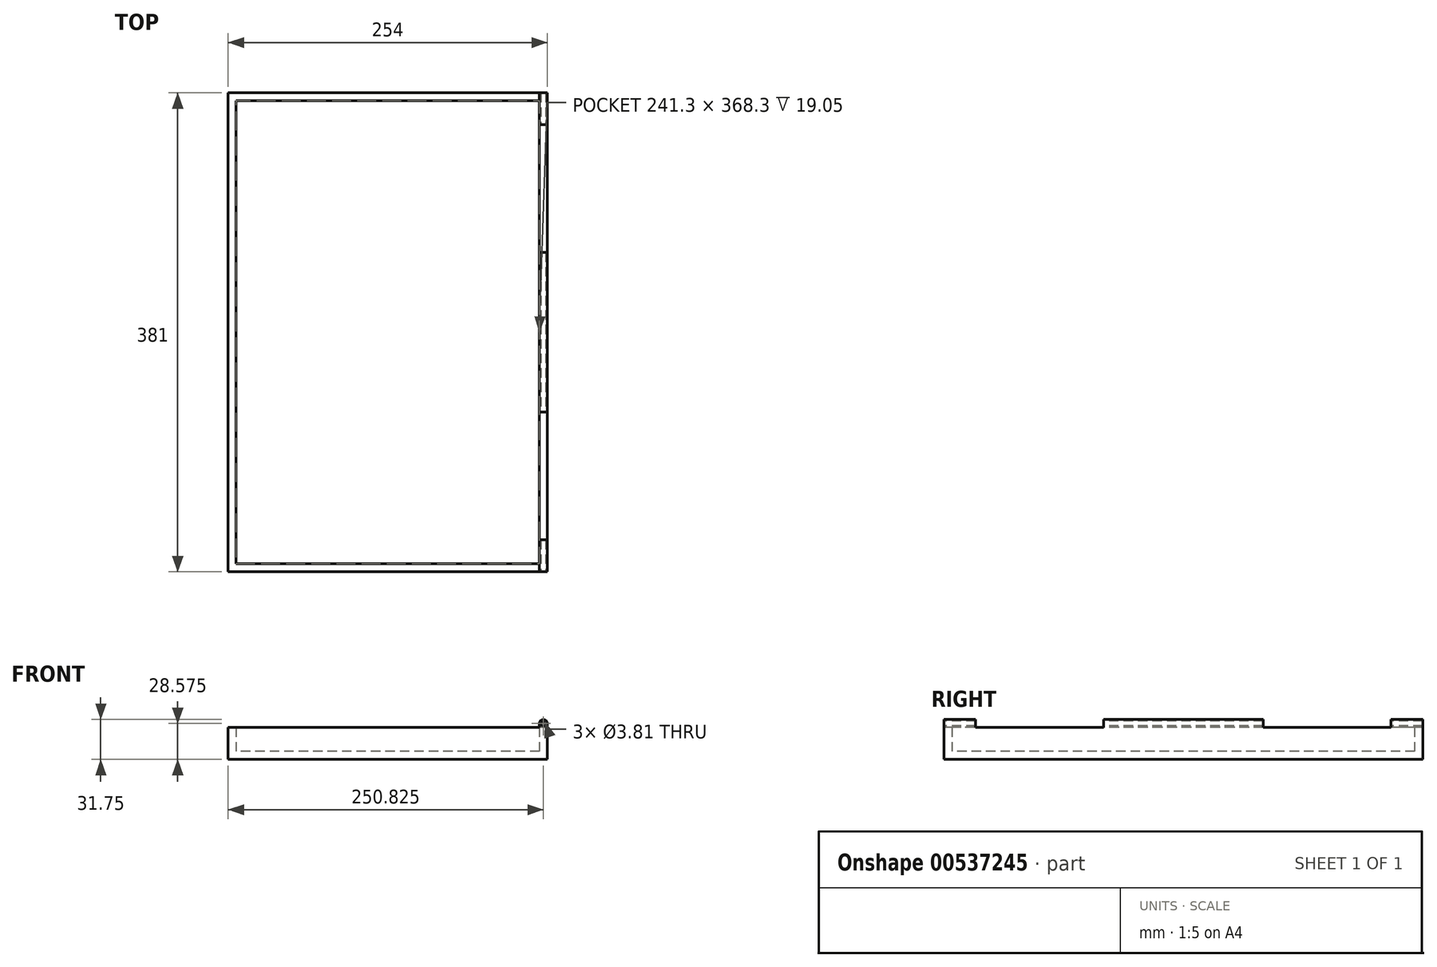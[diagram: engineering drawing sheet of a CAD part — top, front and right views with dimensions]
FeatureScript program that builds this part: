
annotation { "Feature Type Name" : "Feature", "Feature Type Description" : "" }
export const myFeature = defineFeature(function(context is Context, id is Id, definition is map)
    precondition{}
    {
        {
            var Q0;
            Q0=qCreatedBy(makeId("Top.planeOp"),FACE);
            var sketch = newSketch(context, id + "F0", { "sketchPlane" : qUnion([Q0])});
            skLineSegment(sketch, "E0.bottom", {"start": v(127, 190.5) * mm, "end": v(-127, 190.5) * mm});
            skLineSegment(sketch, "E0.top", {"start": v(127, -190.5) * mm, "end": v(-127, -190.5) * mm});
            skLineSegment(sketch, "E0.left", {"start": v(127, 190.5) * mm, "end": v(127, -190.5) * mm});
            skLineSegment(sketch, "E0.right", {"start": v(-127, 190.5) * mm, "end": v(-127, -190.5) * mm});
            skPoint(sketch, "E0.middle", {"position": v(0, 0) * mm});
            skLineSegment(sketch, "E1.0", {"start": v(120.65, -184.15) * mm, "end": v(-120.65, -184.15) * mm});
            skLineSegment(sketch, "E1.1", {"start": v(120.65, 184.15) * mm, "end": v(120.65, -184.15) * mm});
            skLineSegment(sketch, "E1.2", {"start": v(120.65, 184.15) * mm, "end": v(-120.65, 184.15) * mm});
            skLineSegment(sketch, "E1.3", {"start": v(-120.65, 184.15) * mm, "end": v(-120.65, -184.15) * mm});
            skSolve(sketch);
        }
        {
            var Q0;
            Q0 = qSketchRegion(id + "F0", true);
            extrude(context, id + "F1", {"entities" : qUnion([Q0]), "depth" : 25.4 * mm, "offsetDistance" : 25.4 * mm});
        }
        {
            var Q0;
            Q0=makeQuery(id+"F0.imprint","IMPRINT",FACE,{"disambiguationData":[TD([[makeQuery(id+"F0.imprint","IMPRINT",EDGE,{"derivedFrom":sQuery(id+"F0.wireOp",EDGE,"E1.0")}),-1.0]])]});
            extrude(context, id + "F2", {"entities" : qUnion([Q0]), "operationType" : NewBodyOperationType.ADD, "depth" : 6.35 * mm, "offsetDistance" : 25.4 * mm});
        }
        {
            var Q0;
            Q0=makeQuery(id+"F1.opExtrude","SWEPT_FACE",FACE,{"disambiguationData":[OSD([sQuery(id+"F0.wireOp",EDGE,"E0.top")])]});
            var sketch = newSketch(context, id + "F3", { "sketchPlane" : qUnion([Q0])});
            skLineSegment(sketch, "E2", {"start": v(127, 25.4) * mm, "end": v(120.65, 25.4) * mm});
            skArc(sketch, "E3", {"start": v(127, 28.58) * mm, "mid": v(123.83, 31.75) * mm, "end": v(120.65, 28.58) * mm});
            skLineSegment(sketch, "E4", {"start": v(127, 25.4) * mm, "end": v(127, 28.58) * mm});
            skLineSegment(sketch, "E5", {"start": v(120.65, 25.4) * mm, "end": v(120.65, 28.58) * mm});
            skCircle(sketch, "E6.0", {"center": v(123.83, 28.58) * mm, "radius": 1.9 * mm});
            skPoint(sketch, "E7.orphan", {"position": v(123.83, 25.4) * mm});
            skSolve(sketch);
        }
        {
            var Q0;
            Q0=makeQuery(id+"F3.imprint","IMPRINT",FACE,{"disambiguationData":[TD([[makeQuery(id+"F3.imprint","IMPRINT",EDGE,{"derivedFrom":sQuery(id+"F3.wireOp",EDGE,"E2")}),-1.0]])]});
            extrude(context, id + "F4", {"entities" : qUnion([Q0]), "operationType" : NewBodyOperationType.ADD, "oppositeDirection" : true, "depth" : 254 * mm, "offsetDistance" : 25.4 * mm, "hasSecondDirection" : true, "secondDirectionOppositeDirection" : true, "secondDirectionDepth" : 127 * mm});
        }
        {
            var Q0;
            Q0 = qSketchRegion(id + "F3", true);
            extrude(context, id + "F5", {"entities" : qUnion([Q0]), "operationType" : NewBodyOperationType.ADD, "oppositeDirection" : true, "depth" : 25.4 * mm, "offsetDistance" : 25.4 * mm});
        }
        {
            var Q0;
            Q0 = qSketchRegion(id + "F3", true);
            extrude(context, id + "F6", {"entities" : qUnion([Q0]), "operationType" : NewBodyOperationType.ADD, "oppositeDirection" : true, "depth" : 381 * mm, "offsetDistance" : 25.4 * mm, "hasSecondDirection" : true, "secondDirectionOppositeDirection" : true, "secondDirectionDepth" : 355.6 * mm});
        }
    });
